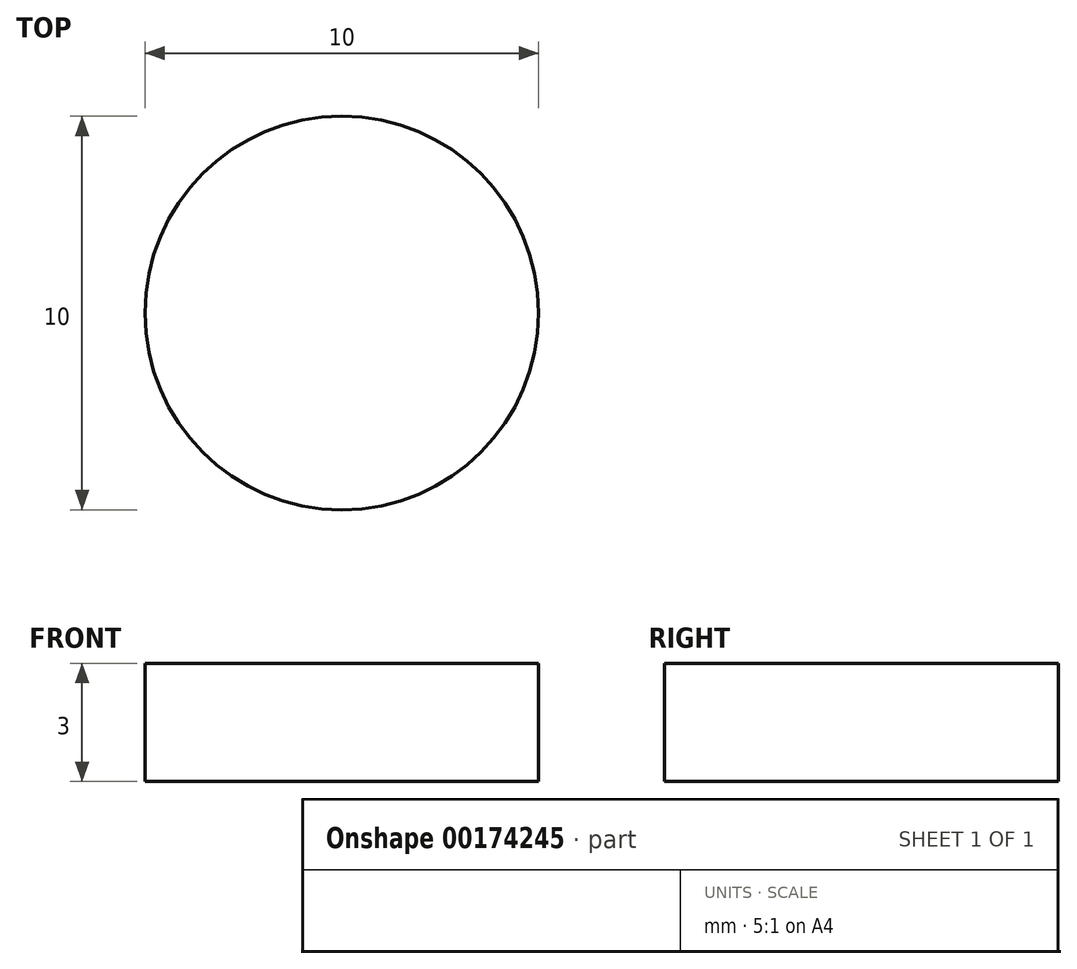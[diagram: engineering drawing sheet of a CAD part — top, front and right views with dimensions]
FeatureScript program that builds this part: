
annotation { "Feature Type Name" : "Feature", "Feature Type Description" : "" }
export const myFeature = defineFeature(function(context is Context, id is Id, definition is map)
    precondition{}
    {
        {
            var Q0;
            Q0=qCreatedBy(makeId("Top.planeOp"),FACE);
            var sketch = newSketch(context, id + "F0", { "sketchPlane" : qUnion([Q0])});
            skCircle(sketch, "E0", {"center": v(0, 0) * mm, "radius": 5 * mm});
            skSolve(sketch);
        }
        {
            var Q0;
            Q0 = qSketchRegion(id + "F0", true);
            extrude(context, id + "F1", {"entities" : qUnion([Q0]), "depth" : 3 * mm});
        }
    });
